# Revit family: Electronics_Expansion-Inputs_Biamp_Vocia_Telephone-Paging-Adapter_POTS-1__
name_source: partatom
category: Communication Devices
units: mm (PartAtom-declared; Revit-internal decimal feet)

## family parameters
Cut with Voids When Loaded = No
Host = Face
Maintain Annotation Orientation = No
OmniClass Number = 23.85.10.11.14
OmniClass Title = Audio Equipment
Part Type = Normal
Room Calculation Point = No
Round Connector Dimension = Use Diameter
Shared = No

## types (1)
- POTS-1
    Altitude = 0-10,000 ft (0-3000m) MSL
    Apparent Load = 30 VA
    Compliance = FCC Part 15B (USA) FCC Part 68 (USA) Industry Canada CS-03 (Canada) CE marked (Europe) RCM (Australia) EAC (Eurasian Customs Union) RoHS Directive (Europe)
    Connector Description = 24V DC; <100mV Ripple (Max 30W)
    Default Elevation = 48 "
    Depth = 8.98 "
    Description = Vocia® POTS-1 Telephone Paging Adapter
    Dynamic Range = 67dB
    Frequency Response = 250Hz-3.4kHz
    Height = 1.73 "
    Housing Material = Biamp - Metal - Silver
    Humidity = 0-95% relative humidity (non-condensing)
    Manufacturer = Biamp
    Max Power Consumption = 30 W
    Model = Vocia POTS-1
    Network Audio = 20-bits, 48kHz, 5-1/3ms (fixed)
    Network Connection = Dual RJ-45 with shielded Ethernet (CAT5, CAT5e, CAT6, or CAT7)
    Number of Poles = 1
    Power Factor = 1
    Product Documentation Link = https://downloads.biamp.com
    Product Page URL = https://www.biamp.com
    Product data url = https://www.bimobject.com
    Ringer Equivalency Number (REN) = 0.2
    THD+N = 250Hz – 2kHz: < 0.3%
    Temperature Range = 18 - 108° F (-8  –  42° C)
    TransHybrid Balance = 30dB
    URL = https://www.biamp.com
    Voltage = 24 V
    Weight = 2.40 lbf
    Width = 19.02 "

## geometry (parser evidence)
native form markers: Sweep x4
no freeform markers — native parametric forms only
